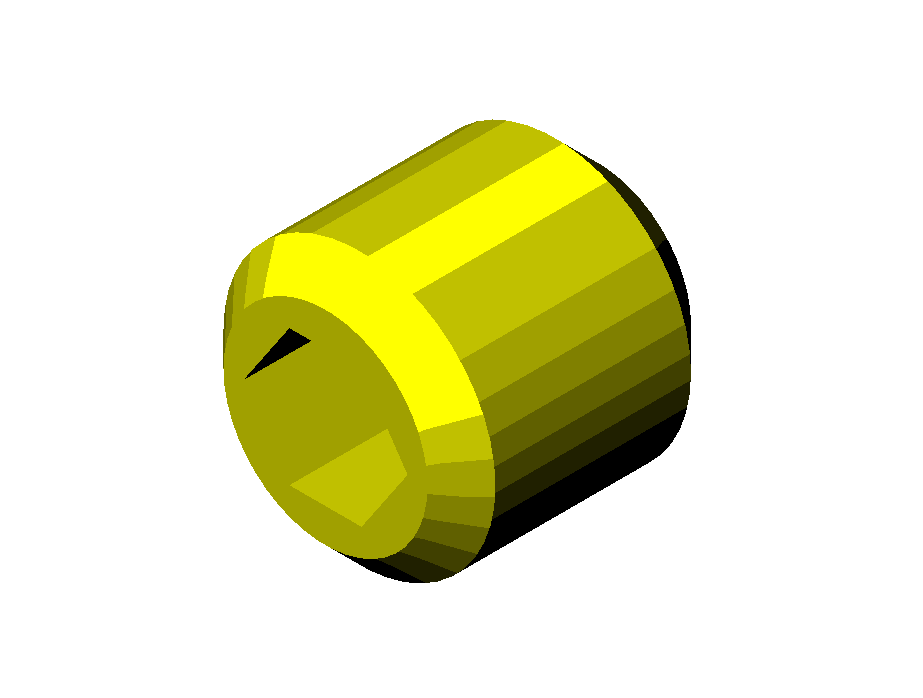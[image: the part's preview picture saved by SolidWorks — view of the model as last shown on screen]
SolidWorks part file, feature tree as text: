
SOLIDWORKS PART (.sldprt)
format: sldprt  version: not decoded by parser v0  size: 116,224 bytes
history: native  units: mm
features: plane x3, sketch x2, chamfer x2, material x1, extrude x1, cut_extrude x1 (+10 scaffold rows collapsed)
feature tree (20):
  scaffold x10  (default folders/planes/origin — collapsed)
  material  "Matériau <non spécifié>"
  plane  "Plane1"
  plane  "Plane2"
  plane  "Plane3"
  sketch  "Esquisse1"  dims[D1=8.0mm]
  extrude  "Base-Extrusion"  Depth=8mm
  chamfer  "Chanfrein1"  Distance=1.25mm Angle=45deg
  sketch  "Esquisse2"  dims[D1=4.0mm D2=4.0mm]
  cut_extrude  "Enlèv. mat.-Extru.1"  Depth=4mm
  chamfer  "Chanfrein2"  Distance=1mm Angle=45deg
decode coverage: 6 of 6 modeling features carry decoded parameters
note: suppression state not decoded; provenance and decode notes live in map.json
